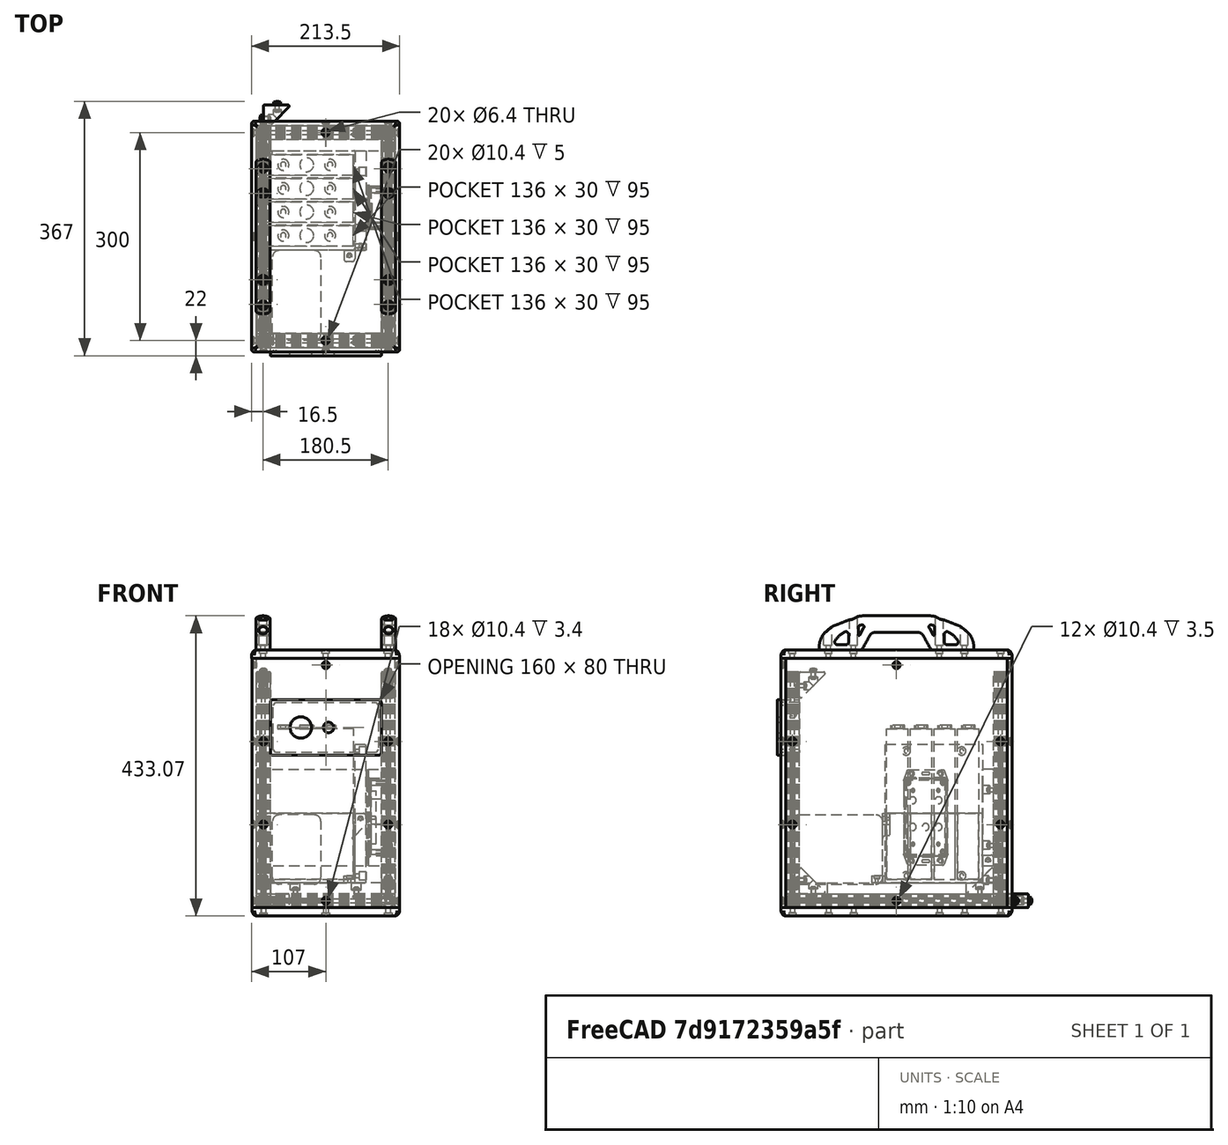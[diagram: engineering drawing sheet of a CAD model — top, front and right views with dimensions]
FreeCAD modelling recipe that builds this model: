
FCSTD DOCUMENT  (FreeCAD 0.17R9796 (Git))
Label: UPKframeNG2j_noplexi
License: All rights reserved
LicenseURL: http://en.wikipedia.org/wiki/All_rights_reserved
objects: Part::Feature×74, Part::FeaturePython×24, Part::Compound×12, App::FeaturePython×8, App::Part×6, Part::Cylinder×5, Part::Box×4, Part::Cut×4, PartDesign::Body×2, PartDesign::Pocket×1, Part::Fillet×1, Part::MultiFuse×1
note: 129 computed .brp shape members not serialized (recipe doc carries the construction recipe); baked Part::Feature solids carry a one-line shape summary decoded from their .brp

FEATURE [Part::Feature] Pocket003001  label="tslot32con"
  Placement = pos=(0,10,10) rot=(1,0,0;1.5708rad)
  shape: bbox 20 x 320 x 20 mm, 150 faces (baked)
FEATURE [Part::Feature] Pocket003002  label="tslot16"
  Placement = pos=(10,0,10) rot=(0,1,0;1.5708rad)
  shape: bbox 160 x 20 x 20 mm, 94 faces (baked)
FEATURE [Part::Feature] Pocket003006  label="tslot16_001"
  Placement = pos=(10,-300,10) rot=(0,1,0;1.5708rad)
  shape: bbox 160 x 20 x 20 mm, 94 faces (baked)
FEATURE [Part::Feature] Pocket003007  label="tslot32con_001"
  Placement = pos=(180,-310,10) rot=(0,0.707107,0.707107;3.14159rad)
  shape: bbox 20 x 320 x 20 mm, 150 faces (baked)
FEATURE [Part::FeaturePython] Screw  label="M6x25-Screw"  # Fasteners workbench fastener (typed FeaturePython)
  Placement = pos=(-4,0,10) rot=(0,-1,0;1.5708rad)
  diameter = 7
  invert = false
  length = 6
  matchOuter = false
  offset = 0
  thread = false
  type = 15
FEATURE [Part::FeaturePython] Screw001  label="M6x25-Screw004"  # Fasteners workbench fastener (typed FeaturePython)
  Placement = pos=(-4,-300,10) rot=(0,-1,0;1.5708rad)
  diameter = 7
  invert = false
  length = 6
  matchOuter = false
  offset = 0
  thread = false
  type = 15
FEATURE [Part::FeaturePython] Screw002  label="M6x25-Screw005"  # Fasteners workbench fastener (typed FeaturePython)
  Placement = pos=(184,0,10) rot=(0,1,0;1.5708rad)
  diameter = 7
  invert = false
  length = 6
  matchOuter = false
  offset = 0
  thread = false
  type = 15
FEATURE [Part::FeaturePython] Screw004  label="M6x25-Screw006"  # Fasteners workbench fastener (typed FeaturePython)
  Placement = pos=(184,-300,10) rot=(0,1,0;1.5708rad)
  diameter = 7
  invert = false
  length = 6
  matchOuter = false
  offset = 0
  thread = false
  type = 15
FEATURE [App::Part] Part  label="lower_frame"
  Group = -> [Pocket003001,Pocket003002,Pocket003006,Pocket003007,Screw,Screw001,Screw002,Screw004]
  License = CC BY 3.0
  LicenseURL = http://creativecommons.org/licenses/by/3.0/
  Origin = -> PartOrigin
FEATURE [Part::Feature] Pocket003008  label="tslot32con001"
  Placement = pos=(0,10,10) rot=(1,0,0;1.5708rad)
  shape: bbox 20 x 320 x 20 mm, 150 faces (baked)
FEATURE [Part::Feature] Pocket003009  label="tslot041"
  Placement = pos=(10,0,10) rot=(0,1,0;1.5708rad)
  shape: bbox 160 x 20 x 20 mm, 94 faces (baked)
FEATURE [Part::Feature] Pocket003010  label="tslot16_002"
  Placement = pos=(10,-300,10) rot=(0,1,0;1.5708rad)
  shape: bbox 160 x 20 x 20 mm, 94 faces (baked)
FEATURE [Part::Feature] Pocket003011  label="tslot32con_002"
  Placement = pos=(180,-310,10) rot=(0,0.707107,0.707107;3.14159rad)
  shape: bbox 20 x 320 x 20 mm, 150 faces (baked)
FEATURE [Part::FeaturePython] Screw005  label="M6x25-Screw007"  # Fasteners workbench fastener (typed FeaturePython)
  Placement = pos=(-4,0,10) rot=(0,-1,0;1.5708rad)
  diameter = 7
  invert = false
  length = 6
  matchOuter = false
  offset = 0
  thread = false
  type = 15
FEATURE [Part::FeaturePython] Screw006  label="M6x25-Screw008"  # Fasteners workbench fastener (typed FeaturePython)
  Placement = pos=(-4,-300,10) rot=(0,-1,0;1.5708rad)
  diameter = 7
  invert = false
  length = 6
  matchOuter = false
  offset = 0
  thread = false
  type = 15
FEATURE [Part::FeaturePython] Screw007  label="M6x25-Screw009"  # Fasteners workbench fastener (typed FeaturePython)
  Placement = pos=(184,0,10) rot=(0,1,0;1.5708rad)
  diameter = 7
  invert = false
  length = 6
  matchOuter = false
  offset = 0
  thread = false
  type = 15
FEATURE [Part::FeaturePython] Screw008  label="M6x25-Screw010"  # Fasteners workbench fastener (typed FeaturePython)
  Placement = pos=(184,-300,10) rot=(0,1,0;1.5708rad)
  diameter = 7
  invert = false
  length = 6
  matchOuter = false
  offset = 0
  thread = false
  type = 15
FEATURE [App::Part] Part001  label="upper_frame"
  Group = -> [Pocket003008,Pocket003009,Pocket003010,Pocket003011,Screw005,Screw006,Screw007,Screw008]
  License = CC BY 3.0
  LicenseURL = http://creativecommons.org/licenses/by/3.0/
  Origin = -> PartOrigin001
  Placement = pos=(0,0,340) rot=(0,0,1;0rad)
FEATURE [Part::Feature] Fillet004001  label="Fillet005"
  shape: bbox 37.5 x 37.5 x 20 mm, 26 faces (baked)
FEATURE [Part::FeaturePython] Screw009  label="M6x12-Screw"  # Fasteners workbench fastener (typed FeaturePython)
  Placement = pos=(7,20,10) rot=(0,1,0;1.5708rad)
  diameter = 4
  invert = false
  length = 1
  matchOuter = false
  offset = 0
  thread = false
  type = 20
FEATURE [Part::Feature] Body001  label="m6nutplate"
  Placement = pos=(-1.5,15,5) rot=(0,-1,0;1.5708rad)
  shape: bbox 3 x 10 x 10 mm, 9 faces (baked)
FEATURE [App::Part] Part002  label="cornerstonescrewnut"
  License = CC BY 3.0
  LicenseURL = http://creativecommons.org/licenses/by/3.0/
  Origin = -> PartOrigin002
  Placement = pos=(10,-50,20) rot=(0,-1,0;1.5708rad)
FEATURE [Part::FeaturePython] Screw010  label="M6x12-Screw001"  # Fasteners workbench fastener (typed FeaturePython)
  Placement = pos=(20,33,10) rot=(1,0,0;1.5708rad)
  diameter = 4
  invert = false
  length = 1
  matchOuter = false
  offset = 0
  thread = false
  type = 20
FEATURE [Part::Feature] Body002  label="m6nutplate001"
  Placement = pos=(15,41.5,5) rot=(0.57735,0.57735,0.57735;4.18879rad)
  shape: bbox 10 x 3 x 10 mm, 9 faces (baked)
FEATURE [Part::Feature] Fillet004002  label="Fillet006"
  shape: bbox 37.5 x 37.5 x 20 mm, 26 faces (baked)
FEATURE [Part::FeaturePython] Screw011  label="M6x12-Screw002"  # Fasteners workbench fastener (typed FeaturePython)
  Placement = pos=(7,20,10) rot=(0,1,0;1.5708rad)
  diameter = 4
  invert = false
  length = 1
  matchOuter = false
  offset = 0
  thread = false
  type = 20
FEATURE [Part::Feature] Body003  label="m6nutplate002"
  Placement = pos=(-1.5,15,5) rot=(0,-1,0;1.5708rad)
  shape: bbox 3 x 10 x 10 mm, 9 faces (baked)
FEATURE [Part::FeaturePython] Screw012  label="M6x12-Screw003"  # Fasteners workbench fastener (typed FeaturePython)
  Placement = pos=(20,33,10) rot=(1,0,0;1.5708rad)
  diameter = 4
  invert = false
  length = 1
  matchOuter = false
  offset = 0
  thread = false
  type = 20
FEATURE [Part::Feature] Body004  label="m6nutplate003"
  Placement = pos=(15,41.5,5) rot=(0.57735,0.57735,0.57735;4.18879rad)
  shape: bbox 10 x 3 x 10 mm, 9 faces (baked)
FEATURE [App::Part] Part003  label="cornerstonescrewnut001"
  Group = -> [Body003,Screw011,Fillet004002,Screw012,Body004,PartOrigin002,Body001,Screw009,Fillet004001,Screw010,Body002,Part002]
  License = CC BY 3.0
  LicenseURL = http://creativecommons.org/licenses/by/3.0/
  Origin = -> PartOrigin003
  Placement = pos=(190,-50,20) rot=(0,-1,0;1.5708rad)
FEATURE [Part::Feature] Fillet004003  label="Fillet004005006"
  shape: bbox 37.5 x 37.5 x 20 mm, 26 faces (baked)
FEATURE [Part::FeaturePython] Screw013  label="M6x12-Screw004"  # Fasteners workbench fastener (typed FeaturePython)
  Placement = pos=(7,20,10) rot=(0,1,0;1.5708rad)
  diameter = 4
  invert = false
  length = 1
  matchOuter = false
  offset = 0
  thread = false
  type = 20
FEATURE [Part::Feature] Body005  label="m6nutplate004"
  Placement = pos=(-1.5,15,5) rot=(0,-1,0;1.5708rad)
  shape: bbox 3 x 10 x 10 mm, 9 faces (baked)
FEATURE [Part::FeaturePython] Screw014  label="M6x12-Screw005"  # Fasteners workbench fastener (typed FeaturePython)
  Placement = pos=(20,33,10) rot=(1,0,0;1.5708rad)
  diameter = 4
  invert = false
  length = 1
  matchOuter = false
  offset = 0
  thread = false
  type = 20
FEATURE [Part::Feature] Body006  label="m6nutplate005"
  Placement = pos=(15,41.5,5) rot=(0.57735,0.57735,0.57735;4.18879rad)
  shape: bbox 10 x 3 x 10 mm, 9 faces (baked)
FEATURE [App::Part] Part004  label="cornerstonescrewnut002"
  Group = -> [Body005,Screw013,Fillet004003,Screw014,Body006]
  License = CC BY 3.0
  LicenseURL = http://creativecommons.org/licenses/by/3.0/
  Origin = -> PartOrigin004
  Placement = pos=(-10,-50,340) rot=(0,1,0;1.5708rad)
FEATURE [Part::Feature] Fillet004004  label="Fillet008"
  shape: bbox 37.5 x 37.5 x 20 mm, 26 faces (baked)
FEATURE [Part::FeaturePython] Screw015  label="M6x12-Screw006"  # Fasteners workbench fastener (typed FeaturePython)
  Placement = pos=(7,20,10) rot=(0,1,0;1.5708rad)
  diameter = 4
  invert = false
  length = 1
  matchOuter = false
  offset = 0
  thread = false
  type = 20
FEATURE [Part::Feature] Body007  label="m6nutplate006"
  Placement = pos=(-1.5,15,5) rot=(0,-1,0;1.5708rad)
  shape: bbox 3 x 10 x 10 mm, 9 faces (baked)
FEATURE [Part::FeaturePython] Screw016  label="M6x12-Screw007"  # Fasteners workbench fastener (typed FeaturePython)
  Placement = pos=(20,33,10) rot=(1,0,0;1.5708rad)
  diameter = 4
  invert = false
  length = 1
  matchOuter = false
  offset = 0
  thread = false
  type = 20
FEATURE [Part::Feature] Body008  label="m6nutplate007"
  Placement = pos=(15,41.5,5) rot=(0.57735,0.57735,0.57735;4.18879rad)
  shape: bbox 10 x 3 x 10 mm, 9 faces (baked)
FEATURE [App::Part] Part005  label="cornerstonescrewnut003"
  Group = -> [Body007,Screw015,Fillet004004,Screw016,Body008]
  License = CC BY 3.0
  LicenseURL = http://creativecommons.org/licenses/by/3.0/
  Origin = -> PartOrigin005
  Placement = pos=(170,-50,340) rot=(0,1,0;1.5708rad)
FEATURE [Part::Feature] Body009001  label="m6nutplate010"
  Placement = pos=(-1.5,15,5) rot=(0,-1,0;1.5708rad)
  shape: bbox 3 x 10 x 10 mm, 9 faces (baked)
FEATURE [Part::Feature] Body010001  label="m6nutplate011"
  Placement = pos=(15,41.5,5) rot=(0.57735,0.57735,0.57735;4.18879rad)
  shape: bbox 10 x 3 x 10 mm, 9 faces (baked)
FEATURE [Part::Feature] Screw018001  label="M6x12-Screw010"
  Placement = pos=(20,33,10) rot=(1,0,0;1.5708rad)
  shape: bbox 10.5 x 15.3 x 10.5 mm, 15 faces (baked)
FEATURE [Part::Feature] Screw017001  label="M6x12-Screw011"
  Placement = pos=(7,20,10) rot=(0,1,0;1.5708rad)
  shape: bbox 15.3 x 10.5 x 10.5 mm, 15 faces (baked)
FEATURE [Part::Feature] Fillet004005001  label="Fillet010"
  shape: bbox 37.5 x 37.5 x 20 mm, 26 faces (baked)
FEATURE [Part::Compound] Compound
  Links = -> [Body009001,Fillet004005001,Screw017001,Body010001,Screw018001]
  Placement = pos=(10,-250,340) rot=(0.707107,0,-0.707107;3.14159rad)
FEATURE [Part::Feature] Body010002  label="m6nutplate012"
  Placement = pos=(-1.5,15,5) rot=(0,-1,0;1.5708rad)
  shape: bbox 3 x 10 x 10 mm, 9 faces (baked)
FEATURE [Part::Feature] Body010003  label="m6nutplate013"
  Placement = pos=(15,41.5,5) rot=(0.57735,0.57735,0.57735;4.18879rad)
  shape: bbox 10 x 3 x 10 mm, 9 faces (baked)
FEATURE [Part::Feature] Screw018002  label="M6x12-Screw012"
  Placement = pos=(20,33,10) rot=(1,0,0;1.5708rad)
  shape: bbox 10.5 x 15.3 x 10.5 mm, 15 faces (baked)
FEATURE [Part::Feature] Screw018003  label="M6x12-Screw013"
  Placement = pos=(7,20,10) rot=(0,1,0;1.5708rad)
  shape: bbox 15.3 x 10.5 x 10.5 mm, 15 faces (baked)
FEATURE [Part::Feature] Fillet004005002  label="Fillet011"
  shape: bbox 37.5 x 37.5 x 20 mm, 26 faces (baked)
FEATURE [Part::Compound] Compound001
  Links = -> [Body010002,Fillet004005002,Screw018003,Body010003,Screw018002]
  Placement = pos=(190,-250,340) rot=(0.707107,0,-0.707107;3.14159rad)
FEATURE [Part::Feature] Body010004  label="m6nutplate014"
  Placement = pos=(-1.5,15,5) rot=(0,-1,0;1.5708rad)
  shape: bbox 3 x 10 x 10 mm, 9 faces (baked)
FEATURE [Part::Feature] Body010005  label="m6nutplate015"
  Placement = pos=(15,41.5,5) rot=(0.57735,0.57735,0.57735;4.18879rad)
  shape: bbox 10 x 3 x 10 mm, 9 faces (baked)
FEATURE [Part::Feature] Screw018004  label="M6x12-Screw014"
  Placement = pos=(20,33,10) rot=(1,0,0;1.5708rad)
  shape: bbox 10.5 x 15.3 x 10.5 mm, 15 faces (baked)
FEATURE [Part::Feature] Screw018005  label="M6x12-Screw015"
  Placement = pos=(7,20,10) rot=(0,1,0;1.5708rad)
  shape: bbox 15.3 x 10.5 x 10.5 mm, 15 faces (baked)
FEATURE [Part::Feature] Fillet004005003  label="Fillet012"
  shape: bbox 37.5 x 37.5 x 20 mm, 26 faces (baked)
FEATURE [Part::Compound] Compound002
  Links = -> [Body010004,Fillet004005003,Screw018005,Body010005,Screw018004]
  Placement = pos=(10,-290,60) rot=(0.57735,0.57735,-0.57735;4.18879rad)
FEATURE [Part::Feature] Body010006  label="m6nutplate016"
  Placement = pos=(-1.5,15,5) rot=(0,-1,0;1.5708rad)
  shape: bbox 3 x 10 x 10 mm, 9 faces (baked)
FEATURE [Part::Feature] Body010007  label="m6nutplate017"
  Placement = pos=(15,41.5,5) rot=(0.57735,0.57735,0.57735;4.18879rad)
  shape: bbox 10 x 3 x 10 mm, 9 faces (baked)
FEATURE [Part::Feature] Screw018006  label="M6x12-Screw016"
  Placement = pos=(20,33,10) rot=(1,0,0;1.5708rad)
  shape: bbox 10.5 x 15.3 x 10.5 mm, 15 faces (baked)
FEATURE [Part::Feature] Screw018007  label="M6x12-Screw017"
  Placement = pos=(7,20,10) rot=(0,1,0;1.5708rad)
  shape: bbox 15.3 x 10.5 x 10.5 mm, 15 faces (baked)
FEATURE [Part::Feature] Fillet004005004  label="Fillet013"
  shape: bbox 37.5 x 37.5 x 20 mm, 26 faces (baked)
FEATURE [Part::Compound] Compound003
  Links = -> [Body010006,Fillet004005004,Screw018007,Body010007,Screw018006]
  Placement = pos=(190,-290,60) rot=(0.57735,0.57735,-0.57735;4.18879rad)
FEATURE [Part::Feature] Pocket001001  label="tslot32"
  Placement = pos=(0,0,20) rot=(0,0,1;0rad)
  shape: bbox 20 x 20 x 320 mm, 94 faces (baked)
FEATURE [Part::Feature] Body010008  label="m6nutplate018"
  Placement = pos=(-1.5,15,5) rot=(0,-1,0;1.5708rad)
  shape: bbox 3 x 10 x 10 mm, 9 faces (baked)
FEATURE [Part::Feature] Body010009  label="m6nutplate019"
  Placement = pos=(15,41.5,5) rot=(0.57735,0.57735,0.57735;4.18879rad)
  shape: bbox 10 x 3 x 10 mm, 9 faces (baked)
FEATURE [Part::Feature] Screw018008  label="M6x12-Screw018"
  Placement = pos=(20,33,10) rot=(1,0,0;1.5708rad)
  shape: bbox 10.5 x 15.3 x 10.5 mm, 15 faces (baked)
FEATURE [Part::Feature] Screw018009  label="M6x12-Screw019"
  Placement = pos=(7,20,10) rot=(0,1,0;1.5708rad)
  shape: bbox 15.3 x 10.5 x 10.5 mm, 15 faces (baked)
FEATURE [Part::Feature] Fillet004005005  label="Fillet014"
  shape: bbox 37.5 x 37.5 x 20 mm, 26 faces (baked)
FEATURE [Part::Compound] Compound004
  Links = -> [Body010008,Fillet004005005,Screw018009,Body010009,Screw018008]
  Placement = pos=(-10,-10,60) rot=(0.57735,-0.57735,0.57735;4.18879rad)
FEATURE [Part::Feature] Pocket003012  label="tslot32_001"
  Placement = pos=(0,-300,20) rot=(0,0,1;0rad)
  shape: bbox 20 x 20 x 320 mm, 94 faces (baked)
FEATURE [Part::Feature] Pocket003013  label="tslot32_002"
  Placement = pos=(180,0,20) rot=(0,0,1;0rad)
  shape: bbox 20 x 20 x 320 mm, 94 faces (baked)
FEATURE [Part::Feature] Pocket003014  label="tslot32_003"
  Placement = pos=(180,-300,20) rot=(0,0,1;0rad)
  shape: bbox 20 x 20 x 320 mm, 94 faces (baked)
FEATURE [PartDesign::Body] Body010027
FEATURE [Part::FeaturePython] Screw018021  label="M6x12-Screw032"  # Fasteners workbench fastener (typed FeaturePython)
  diameter = 4
  invert = false
  length = 1
  matchOuter = false
  offset = 0
  thread = false
  type = 20
FEATURE [Part::Feature] Body010028  label="m6nutplate032"
  Placement = pos=(5,-5,-8.39) rot=(0,1,0;3.14159rad)
  shape: bbox 10 x 10 x 3 mm, 9 faces (baked)
FEATURE [App::FeaturePython] circularEdgeConstraint009  # a2plus constraint (typed FeaturePython)
  Object1 = Screw
  Object2 = Body001
  SubElement1 = Edge7
  SubElement2 = Edge20
  Type = circularEdge
  directionConstraint = 1
  lockRotation = false
  offset = 0
FEATURE [Part::Compound] Compound017  label="nutplate12screw008"
  Links = -> [Screw018021,circularEdgeConstraint009,Body010028]
  Placement = pos=(10,30,6) rot=(0,0,1;0rad)
FEATURE [Part::FeaturePython] Screw018022  label="M6x12-Screw033"  # Fasteners workbench fastener (typed FeaturePython)
  diameter = 4
  invert = false
  length = 1
  matchOuter = false
  offset = 0
  thread = false
  type = 20
FEATURE [Part::Feature] Body010029  label="m6nutplate033"
  Placement = pos=(5,-5,-8.39) rot=(0,1,0;3.14159rad)
  shape: bbox 10 x 10 x 3 mm, 9 faces (baked)
FEATURE [App::FeaturePython] circularEdgeConstraint010  # a2plus constraint (typed FeaturePython)
  Object1 = Screw
  Object2 = Body001
  SubElement1 = Edge7
  SubElement2 = Edge20
  Type = circularEdge
  directionConstraint = 1
  lockRotation = false
  offset = 0
FEATURE [Part::Compound] Compound018  label="nutplate12screw009"
  Links = -> [Screw018022,circularEdgeConstraint010,Body010029]
  Placement = pos=(10,110,6) rot=(0,0,1;0rad)
FEATURE [Part::FeaturePython] Screw018023  label="M6x12-Screw034"  # Fasteners workbench fastener (typed FeaturePython)
  diameter = 4
  invert = false
  length = 1
  matchOuter = false
  offset = 0
  thread = false
  type = 20
FEATURE [Part::Feature] Body010030  label="m6nutplate034"
  Placement = pos=(5,-5,-8.39) rot=(0,1,0;3.14159rad)
  shape: bbox 10 x 10 x 3 mm, 9 faces (baked)
FEATURE [App::FeaturePython] circularEdgeConstraint011  # a2plus constraint (typed FeaturePython)
  Object1 = Screw
  Object2 = Body001
  SubElement1 = Edge7
  SubElement2 = Edge20
  Type = circularEdge
  directionConstraint = 1
  lockRotation = false
  offset = 0
FEATURE [Part::Compound] Compound019  label="nutplate12screw010"
  Links = -> [Screw018023,circularEdgeConstraint011,Body010030]
  Placement = pos=(190,110,6) rot=(0,0,1;0rad)
FEATURE [Part::FeaturePython] Screw018024  label="M6x12-Screw035"  # Fasteners workbench fastener (typed FeaturePython)
  diameter = 4
  invert = false
  length = 1
  matchOuter = false
  offset = 0
  thread = false
  type = 20
FEATURE [Part::Feature] Body010031  label="m6nutplate035"
  Placement = pos=(5,-5,-8.39) rot=(0,1,0;3.14159rad)
  shape: bbox 10 x 10 x 3 mm, 9 faces (baked)
FEATURE [App::FeaturePython] circularEdgeConstraint012  # a2plus constraint (typed FeaturePython)
  Object1 = Screw
  Object2 = Body001
  SubElement1 = Edge7
  SubElement2 = Edge20
  Type = circularEdge
  directionConstraint = 1
  lockRotation = false
  offset = 0
FEATURE [Part::Compound] Compound020  label="nutplate12screw011"
  Links = -> [Screw018024,circularEdgeConstraint012,Body010031]
  Placement = pos=(190,30,6) rot=(0,0,1;0rad)
FEATURE [Part::Compound] Compound021  label="front_plate"
  Links = -> [Body010027,Compound020,Compound019,Compound017,Compound018]
  Placement = pos=(-10,-10,60) rot=(1,0,0;1.5708rad)
FEATURE [Part::Compound] Compound016  label="bottom_plate"
  Placement = pos=(190,-310,20) rot=(0,0,1;1.5708rad)
FEATURE [PartDesign::Pocket] Pocket003019
  Length = 10
  Placement = pos=(130,-166,235) rot=(0,1,0;1.5708rad)
  Type = 0
FEATURE [Part::Box] Box003  label="MPPT"
  AttacherType = Attacher::AttachEngine3D
  Height = 100
  Length = 130
  Placement = pos=(290,128,10) rot=(0,0,1;0rad)
  Width = 70
FEATURE [Part::Fillet] Fillet007  label="MPPT               "
  Base = -> Box003
  Edges = 12 edges r=10: [Edge1,Edge2,Edge3,Edge4,Edge5,Edge6,Edge7,Edge8,Edge9,Edge10,Edge11,Edge12]
  Placement = pos=(211,-590,24) rot=(0,0,1;1.5708rad)
FEATURE [Part::Feature] Part__Feature1213  label="1591XXBF LID"
  Placement = pos=(153,-86,180) rot=(0.57735,-0.57735,-0.57735;2.0944rad)
  shape: bbox 12.61 x 63.32 x 138 mm, 220 faces (baked)
FEATURE [Part::Feature] Part__Feature1212  label="1591XXB BOX"
  Placement = pos=(0,0,0) rot=(0,0.707107,0.707107;3.14159rad)
  shape: bbox 113.8 x 28.25 x 63.32 mm, 133 faces (baked)
FEATURE [Part::Cylinder] Cylinder  label="Zylinder"
  Angle = 360
  AttacherType = Attacher::AttachEngine3D
  Height = 60
  Placement = pos=(-14,48,18.6) rot=(1,0,0;1.5708rad)
  Radius = 5
FEATURE [Part::Cylinder] Cylinder001  label="Zylinder001"
  Angle = 360
  AttacherType = Attacher::AttachEngine3D
  Height = 60
  Placement = pos=(-14,48,0) rot=(1,0,0;1.5708rad)
  Radius = 5
FEATURE [Part::Cylinder] Cylinder002  label="Zylinder002"
  Angle = 360
  AttacherType = Attacher::AttachEngine3D
  Height = 60
  Placement = pos=(-14,48,-18.66) rot=(1,0,0;1.5708rad)
  Radius = 5
FEATURE [Part::Cylinder] Cylinder003  label="Zylinder003"
  Angle = 360
  AttacherType = Attacher::AttachEngine3D
  Height = 60
  Placement = pos=(24.49,48,18.6) rot=(1,0,0;1.5708rad)
  Radius = 5
FEATURE [Part::Cylinder] Cylinder004  label="Zylinder004"
  Angle = 360
  AttacherType = Attacher::AttachEngine3D
  Height = 60
  Placement = pos=(24.49,48,-18.66) rot=(1,0,0;1.5708rad)
  Radius = 5
FEATURE [Part::MultiFuse] Fusion
  Shapes = -> [Cylinder,Cylinder004,Cylinder003,Cylinder002,Cylinder001]
FEATURE [Part::Cut] Cut
  Base = -> Part__Feature1212
  Tool = -> Fusion
FEATURE [Part::Box] Box002  label="Würfel002"
  AttacherType = Attacher::AttachEngine3D
  Height = 10
  Length = 76
  Placement = pos=(-38,16,-36) rot=(0,0,1;0rad)
  Width = 12.6
FEATURE [Part::Cut] Cut001
  Base = -> Cut
  Tool = -> Box002
FEATURE [Part::Box] Box004  label="Würfel003"
  AttacherType = Attacher::AttachEngine3D
  Height = 10
  Length = 36
  Placement = pos=(-10,9,24) rot=(0,0,1;0rad)
  Width = 20
FEATURE [Part::Cut] Cut002
  Base = -> Cut001
  Tool = -> Box004
FEATURE [Part::Box] Box  label="Würfel"
  AttacherType = Attacher::AttachEngine3D
  Height = 20
  Length = 10
  Placement = pos=(49,23,-6) rot=(0,0,1;0rad)
  Width = 6
FEATURE [Part::Cut] Cut003  label="bms-cover"
  Base = -> Cut002
  Placement = pos=(179,-108,130.5) rot=(0.57735,-0.57735,0.57735;2.0944rad)
  Tool = -> Box
FEATURE [PartDesign::Body] Body010032
FEATURE [Part::FeaturePython] Screw018025  label="M6x12-Screw036"  # Fasteners workbench fastener (typed FeaturePython)
  diameter = 4
  invert = false
  length = 1
  matchOuter = false
  offset = 0
  thread = false
  type = 20
FEATURE [App::FeaturePython] circularEdgeConstraint013  # a2plus constraint (typed FeaturePython)
  Object1 = Screw
  Object2 = Body001
  SubElement1 = Edge7
  SubElement2 = Edge20
  Type = circularEdge
  directionConstraint = 1
  lockRotation = false
  offset = 0
FEATURE [Part::FeaturePython] Screw018026  label="M6x12-Screw037"  # Fasteners workbench fastener (typed FeaturePython)
  diameter = 4
  invert = false
  length = 1
  matchOuter = false
  offset = 0
  thread = false
  type = 20
FEATURE [Part::Feature] Body010034  label="m6nutplate037"
  Placement = pos=(5,-5,-8.39) rot=(0,1,0;3.14159rad)
  shape: bbox 10 x 10 x 3 mm, 9 faces (baked)
FEATURE [App::FeaturePython] circularEdgeConstraint014  # a2plus constraint (typed FeaturePython)
  Object1 = Screw
  Object2 = Body001
  SubElement1 = Edge7
  SubElement2 = Edge20
  Type = circularEdge
  directionConstraint = 1
  lockRotation = false
  offset = 0
FEATURE [Part::FeaturePython] Screw018027  label="M6x12-Screw038"  # Fasteners workbench fastener (typed FeaturePython)
  diameter = 4
  invert = false
  length = 1
  matchOuter = false
  offset = 0
  thread = false
  type = 20
FEATURE [Part::Feature] Body010035  label="m6nutplate038"
  Placement = pos=(5,-5,-8.39) rot=(0,1,0;3.14159rad)
  shape: bbox 10 x 10 x 3 mm, 9 faces (baked)
FEATURE [App::FeaturePython] circularEdgeConstraint015  # a2plus constraint (typed FeaturePython)
  Object1 = Screw
  Object2 = Body001
  SubElement1 = Edge7
  SubElement2 = Edge20
  Type = circularEdge
  directionConstraint = 1
  lockRotation = false
  offset = 0
FEATURE [Part::FeaturePython] Screw018028  label="M6x12-Screw039"  # Fasteners workbench fastener (typed FeaturePython)
  diameter = 4
  invert = false
  length = 1
  matchOuter = false
  offset = 0
  thread = false
  type = 20
FEATURE [Part::Feature] Body010036  label="m6nutplate039"
  Placement = pos=(5,-5,-8.39) rot=(0,1,0;3.14159rad)
  shape: bbox 10 x 10 x 3 mm, 9 faces (baked)
FEATURE [App::FeaturePython] circularEdgeConstraint016  # a2plus constraint (typed FeaturePython)
  Object1 = Screw
  Object2 = Body001
  SubElement1 = Edge7
  SubElement2 = Edge20
  Type = circularEdge
  directionConstraint = 1
  lockRotation = false
  offset = 0
FEATURE [Part::Compound] Compound026  label="bmsmounting_plate"
  Links = -> [Body010032]
  Placement = pos=(132,-26,36) rot=(0.707107,0,0.707107;3.14159rad)
FEATURE [Part::Feature] Body010037  label="batterymount"
  Placement = pos=(-10,-170,36) rot=(0,0,1;0rad)
  shape: bbox 158 x 176 x 100 mm, 72 faces (baked)
FEATURE [Part::Feature] Body010033  label="m6nutplate036"
  Placement = pos=(5,-5,-8.39) rot=(0,1,0;3.14159rad)
  shape: bbox 10 x 10 x 3 mm, 9 faces (baked)
FEATURE [Part::Feature] Body010038  label="cam72"
  Placement = pos=(130,-62,41) rot=(0,0,1;1.5708rad)
  shape: bbox 135.1 x 31 x 222.5 mm, 16 faces (baked)
FEATURE [Part::Feature] Body010039  label="cam72_001"
  Placement = pos=(130,-96,41) rot=(0,0,1;1.5708rad)
  shape: bbox 135.1 x 31 x 222.5 mm, 16 faces (baked)
FEATURE [Part::Feature] Body010040  label="cam72_002"
  Placement = pos=(130,-130,41) rot=(0,0,1;1.5708rad)
  shape: bbox 135.1 x 31 x 222.5 mm, 16 faces (baked)
FEATURE [Part::Feature] Body010041  label="cam72_003"
  Placement = pos=(130,-164,41) rot=(0,0,1;1.5708rad)
  shape: bbox 135.1 x 31 x 222.5 mm, 16 faces (baked)
FEATURE [Part::Feature] Body010042  label="backCover"
  Placement = pos=(-16.5,-310,0) rot=(1,0,0;1.5708rad)
  shape: bbox 213 x 6.5 x 360 mm, 26 faces (baked)
FEATURE [Part::Feature] Body010043  label="frontCover"
  Placement = pos=(196.5,10,0) rot=(0,0.707107,0.707107;3.14159rad)
  shape: bbox 213 x 6.5 x 360 mm, 26 faces (baked)
FEATURE [Part::Feature] Body010044  label="topCover"
  Placement = pos=(-17,-316.5,360) rot=(0,0,1;0rad)
  shape: bbox 213 x 333 x 12 mm, 48 faces (baked)
FEATURE [Part::Feature] Body010045  label="bottomCover"
  Placement = pos=(196.5,-316.5,0) rot=(0,1,0;3.14159rad)
  shape: bbox 213 x 333 x 12 mm, 48 faces (baked)
FEATURE [Part::Feature] Pocket003020  label="sideCover"
  Placement = pos=(190,-310,0) rot=(0.57735,0.57735,0.57735;2.0944rad)
  shape: bbox 6.5 x 320 x 360 mm, 24 faces (baked)
FEATURE [Part::Feature] Pocket003021  label="sideCover001"
  Placement = pos=(-10,10,0) rot=(0.57735,-0.57735,-0.57735;2.0944rad)
  shape: bbox 6.5 x 320 x 360 mm, 24 faces (baked)
FEATURE [Part::Feature] Cut007001  label="handle"
  Placement = pos=(7,-150,372) rot=(0.57735,-0.57735,-0.57735;2.0944rad)
  shape: bbox 20 x 223 x 50.93 mm, 233 faces (baked)
FEATURE [Part::Feature] Cut007002  label="handle001"
  Placement = pos=(188,-150,372) rot=(0.57735,-0.57735,-0.57735;2.0944rad)
  shape: bbox 20 x 223 x 50.93 mm, 233 faces (baked)
FEATURE [Part::Feature] Body010046  label="backCover_ifmount"
  Placement = pos=(-16.5,-310,0) rot=(1,0,0;1.5708rad)
  shape: bbox 213 x 6.5 x 360 mm, 34 faces (baked)
FEATURE [Part::Feature] Body010047  label="ifmount"
  Placement = pos=(10,-322,300) rot=(-1,0,0;1.5708rad)
  shape: bbox 160.7 x 32 x 80.66 mm, 41 faces (baked)
